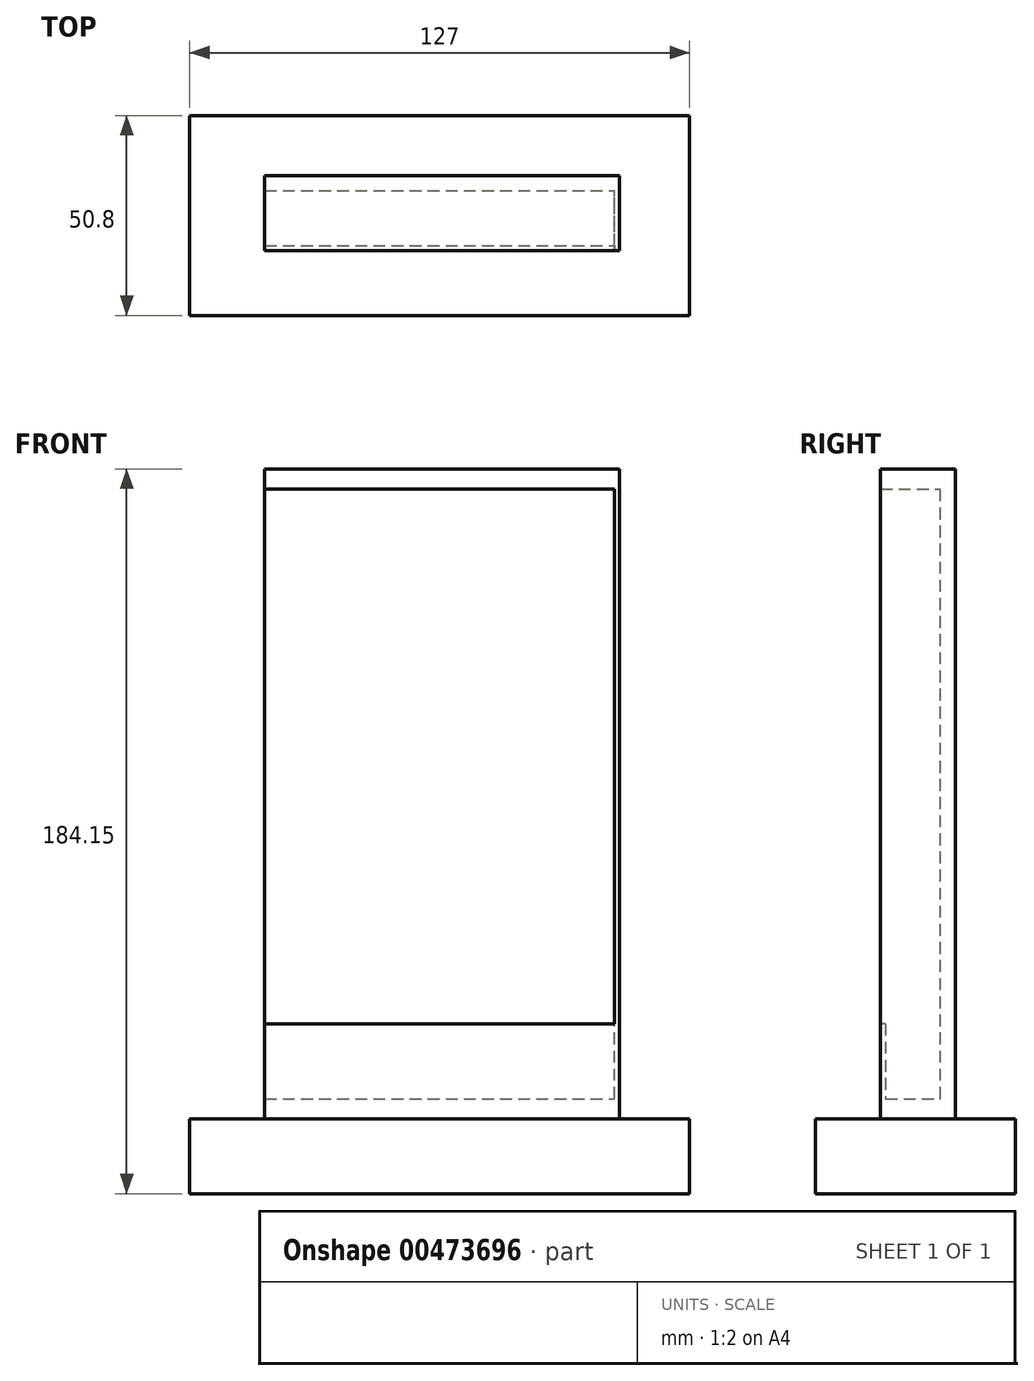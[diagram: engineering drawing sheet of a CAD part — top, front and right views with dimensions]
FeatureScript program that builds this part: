
annotation { "Feature Type Name" : "Feature", "Feature Type Description" : "" }
export const myFeature = defineFeature(function(context is Context, id is Id, definition is map)
    precondition{}
    {
        {
            var Q0;
            Q0=qCreatedBy(makeId("Top.planeOp"),FACE);
            var sketch = newSketch(context, id + "F0", { "sketchPlane" : qUnion([Q0])});
            skLineSegment(sketch, "E0.bottom", {"start": v(0, 50.8) * mm, "end": v(127, 50.8) * mm});
            skLineSegment(sketch, "E0.top", {"start": v(0, 0) * mm, "end": v(127, 0) * mm});
            skLineSegment(sketch, "E0.left", {"start": v(0, 50.8) * mm, "end": v(0, 0) * mm});
            skLineSegment(sketch, "E0.right", {"start": v(127, 50.8) * mm, "end": v(127, 0) * mm});
            skSolve(sketch);
        }
        {
            var Q0;
            Q0=makeQuery(id+"F0.imprint","IMPRINT",FACE,{"disambiguationData":[TD([[makeQuery(id+"F0.imprint","IMPRINT",EDGE,{"derivedFrom":sQuery(id+"F0.wireOp",EDGE,"E0.bottom")}),-1.0]])]});
            extrude(context, id + "F1", {"entities" : qUnion([Q0]), "depth" : 19.05 * mm});
        }
        {
            var Q0;
            Q0=makeQuery(id+"F1.opExtrude","CAP_FACE",FACE,{"disambiguationData":[OSD([sQuery(id+"F0.wireOp",EDGE,"E0.bottom"),sQuery(id+"F0.wireOp",EDGE,"E0.top"),sQuery(id+"F0.wireOp",EDGE,"E0.left"),sQuery(id+"F0.wireOp",EDGE,"E0.right")])],"isStart":false});
            var sketch = newSketch(context, id + "F2", { "sketchPlane" : qUnion([Q0])});
            skLineSegment(sketch, "E1.bottom", {"start": v(19.05, 35.56) * mm, "end": v(107.95, 35.56) * mm});
            skLineSegment(sketch, "E1.top", {"start": v(19.05, 17.78) * mm, "end": v(107.95, 17.78) * mm});
            skLineSegment(sketch, "E1.left", {"start": v(19.05, 35.56) * mm, "end": v(19.05, 17.78) * mm});
            skLineSegment(sketch, "E1.right", {"start": v(107.95, 35.56) * mm, "end": v(107.95, 17.78) * mm});
            skSolve(sketch);
        }
        {
            var Q0;
            Q0 = qSketchRegion(id + "F2", true);
            extrude(context, id + "F3", {"entities" : qUnion([Q0]), "operationType" : NewBodyOperationType.ADD, "depth" : 165.1 * mm});
        }
        {
            var Q0;
            Q0=makeQuery(id+"F3.opExtrude","SWEPT_FACE",FACE,{"disambiguationData":[OSD([sQuery(id+"F2.wireOp",EDGE,"E1.right")])]});
            var sketch = newSketch(context, id + "F4", { "sketchPlane" : qUnion([Q0])});
            skLineSegment(sketch, "E2.bottom", {"start": v(17.78, 24.13) * mm, "end": v(31.75, 24.13) * mm});
            skLineSegment(sketch, "E2.top", {"start": v(17.78, 179.07) * mm, "end": v(31.75, 179.07) * mm});
            skLineSegment(sketch, "E2.left", {"start": v(17.78, 24.13) * mm, "end": v(17.78, 179.07) * mm});
            skLineSegment(sketch, "E2.right", {"start": v(31.75, 24.13) * mm, "end": v(31.75, 179.07) * mm});
            skSolve(sketch);
        }
        {
            var Q0;
            Q0=makeQuery(id+"F4.imprint","IMPRINT",FACE,{"disambiguationData":[TD([[makeQuery(id+"F4.imprint","IMPRINT",EDGE,{"derivedFrom":sQuery(id+"F4.wireOp",EDGE,"E2.bottom")}),1.0]])]});
            extrude(context, id + "F5", {"entities" : qUnion([Q0]), "operationType" : NewBodyOperationType.REMOVE, "oppositeDirection" : true, "depth" : 100.58 * mm});
        }
        {
            var Q0;
            Q0=makeQuery(id+"F1.opExtrude","CAP_FACE",FACE,{"disambiguationData":[OSD([sQuery(id+"F0.wireOp",EDGE,"E0.bottom"),sQuery(id+"F0.wireOp",EDGE,"E0.top"),sQuery(id+"F0.wireOp",EDGE,"E0.left"),sQuery(id+"F0.wireOp",EDGE,"E0.right")])],"isStart":false});
            var sketch = newSketch(context, id + "F6", { "sketchPlane" : qUnion([Q0])});
            skLineSegment(sketch, "E3.bottom", {"start": v(19.05, 17.78) * mm, "end": v(107.95, 17.78) * mm});
            skLineSegment(sketch, "E3.top", {"start": v(19.05, 16.51) * mm, "end": v(107.95, 16.51) * mm});
            skLineSegment(sketch, "E3.left", {"start": v(19.05, 17.78) * mm, "end": v(19.05, 16.51) * mm});
            skLineSegment(sketch, "E3.right", {"start": v(107.95, 17.78) * mm, "end": v(107.95, 16.51) * mm});
            skSolve(sketch);
        }
        {
            var Q0;
            Q0=makeQuery(id+"F6.imprint","IMPRINT",FACE,{"disambiguationData":[TD([[makeQuery(id+"F6.imprint","IMPRINT",EDGE,{"derivedFrom":sQuery(id+"F6.wireOp",EDGE,"E3.bottom")}),-1.0]])]});
            extrude(context, id + "F7", {"entities" : qUnion([Q0]), "operationType" : NewBodyOperationType.ADD, "depth" : 24.13 * mm});
        }
        {
            var Q0;
            Q0=makeQuery(id+"F1.opExtrude","CAP_FACE",FACE,{"disambiguationData":[OSD([sQuery(id+"F0.wireOp",EDGE,"E0.bottom"),sQuery(id+"F0.wireOp",EDGE,"E0.top"),sQuery(id+"F0.wireOp",EDGE,"E0.left"),sQuery(id+"F0.wireOp",EDGE,"E0.right")])],"isStart":false});
            var sketch = newSketch(context, id + "F8", { "sketchPlane" : qUnion([Q0])});
            skLineSegment(sketch, "E4.bottom", {"start": v(107.95, 35.56) * mm, "end": v(109.22, 35.56) * mm});
            skLineSegment(sketch, "E4.top", {"start": v(107.95, 16.51) * mm, "end": v(109.22, 16.51) * mm});
            skLineSegment(sketch, "E4.left", {"start": v(107.95, 35.56) * mm, "end": v(107.95, 16.51) * mm});
            skLineSegment(sketch, "E4.right", {"start": v(109.22, 35.56) * mm, "end": v(109.22, 16.51) * mm});
            skSolve(sketch);
        }
        {
            var Q0;
            Q0 = qSketchRegion(id + "F8", true);
            extrude(context, id + "F9", {"entities" : qUnion([Q0]), "operationType" : NewBodyOperationType.ADD, "depth" : 165.1 * mm});
        }
        {
            var Q0;
            {var subQ2=sQuery(id+"F2.wireOp",EDGE,"E1.top");Q0=makeQuery(id+"F5.boolean.opBoolean","SPLIT",FACE,{"disambiguationData":[TD([makeQuery(id+"F5.opExtrude","SWEPT_FACE",FACE,{"disambiguationData":[OSD([sQuery(id+"F4.wireOp",EDGE,"E2.top")])]})])],"derivedFrom":makeQuery(id+"F3.opExtrude","SWEPT_FACE",FACE,{"disambiguationData":[OSD([subQ2])]})});}
            extrude(context, id + "F10", {"entities" : qUnion([Q0]), "operationType" : NewBodyOperationType.ADD, "depth" : 1.27 * mm});
        }
    });
